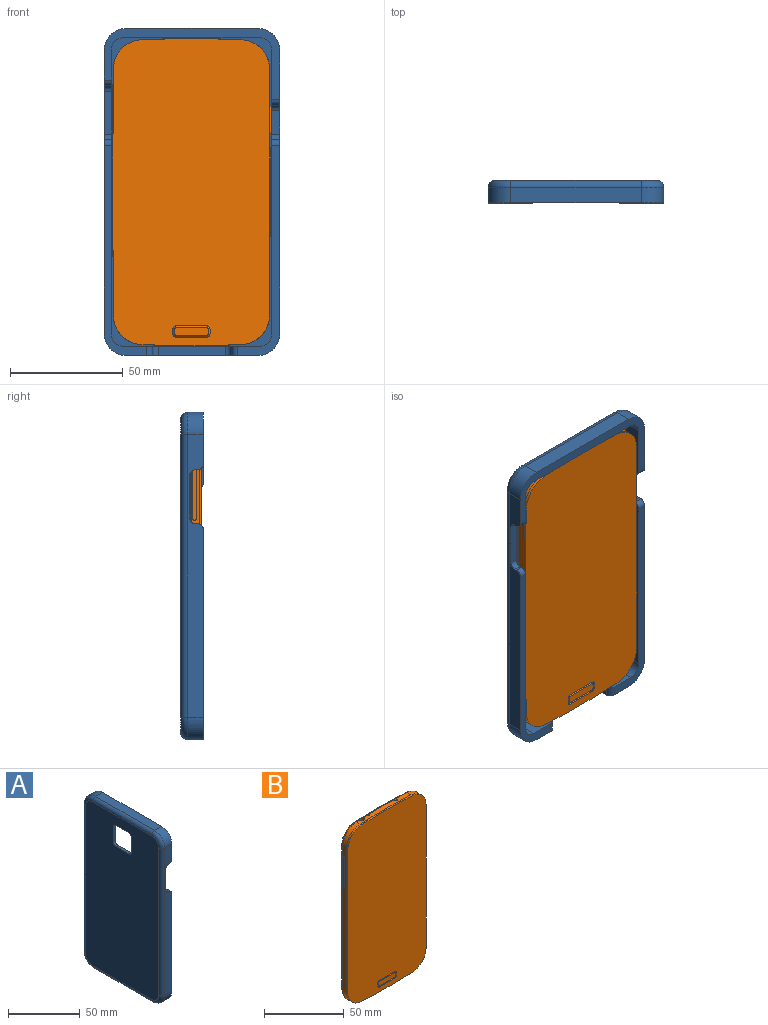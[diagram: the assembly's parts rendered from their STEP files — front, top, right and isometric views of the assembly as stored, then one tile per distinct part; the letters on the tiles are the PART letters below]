
ASSEMBLY  parts=2 mates=1
PART A: 59 faces, bbox 10x79.6x147.1 mm
  f0: plane 93.5x19mm, normal (1,0,0), area 354.7mm2, adj f1,f2,f5,f6,f16,f20,f47,f52
  f1: plane 12.5x7mm, normal (0,0,-1), area 79.8mm2, adj f0,f3,f20,f44,f47,f50
  f2: plane 61x8mm, normal (0,0,1), area 225.5mm2, adj f0,f7,f10,f16,f17,f44,f45,f46
  f3: cylinder r=3mm len=58mm, axis (0,1,0), area 257.2mm2, adj f1,f11,f13,f26,f29,f46,f49,f50
  f4: plane 78x31.7mm, normal (1,0,0), area 463.2mm2, adj f5,f6,f8,f9,f12,f14,f15,f18
  f5: plane 125.5x7mm, normal (0,-1,0), area 734.5mm2, adj f0,f4,f19,f20,f28,f41,f42,f43
  f6: plane 127x8mm, normal (0,1,0), area 872mm2, adj f0,f4,f10,f15,f16,f41,f42,f43
  f7: plane 93.5x19mm, normal (1,0,0), area 399.3mm2, adj f2,f8,f9,f13,f17,f21,f48,f55
  f8: plane 125.5x7mm, normal (0,1,0), area 786.7mm2, adj f4,f7,f21,f22,f24,f38,f39,f40
  f9: plane 127x8mm, normal (0,-1,0), area 924.2mm2, adj f4,f7,f10,f17,f18,f38,f39,f40
  f10: plane 137x71mm, normal (1,0,0), area 9389.3mm2, adj f2,f6,f9,f14,f15,f16,f17,f18
  f11: plane 139.5x72mm, normal (-1,0,0), area 9685.7mm2, adj f3,f23,f24,f25,f26,f27,f28,f29
  f12: plane 58x7mm, normal (0,0,1), area 406mm2, adj f4,f19,f22,f25
  f13: plane 12.5x7mm, normal (0,0,-1), area 79.8mm2, adj f3,f7,f21,f45,f48,f49
  f14: plane 61x8mm, normal (0,0,-1), area 488mm2, adj f4,f10,f15,f18
  f15: cylinder r=5mm len=8mm, axis (1,0,0), area 62.8mm2, adj f4,f6,f10,f14
  f16: cylinder r=5mm len=8mm, axis (-1,0,0), area 62.8mm2, adj f0,f2,f6,f10
  f17: cylinder r=5mm len=8mm, axis (1,0,0), area 62.8mm2, adj f2,f7,f9,f10
  f18: cylinder r=5mm len=8mm, axis (-1,0,0), area 62.8mm2, adj f4,f9,f10,f14
  f19: cylinder r=10mm len=10mm, axis (-1,0,0), area 110mm2, adj f4,f5,f12,f27
  f20: cylinder r=10mm len=10mm, axis (1,0,0), area 110mm2, adj f0,f1,f5,f29
  f21: cylinder r=10mm len=10mm, axis (1,0,0), area 110mm2, adj f7,f8,f13,f26
  f22: cylinder r=10mm len=10mm, axis (-1,0,0), area 110mm2, adj f4,f8,f12,f23
  f23: torus R=7mm, axis (1,0,0), area 66mm2, adj f11,f22,f24,f25
  f24: cylinder r=3mm len=125.5mm, axis (0,0,1), area 591.4mm2, adj f8,f11,f23,f26
  f25: cylinder r=3mm len=58mm, axis (0,-1,0), area 273.3mm2, adj f11,f12,f23,f27
  f26: torus R=7mm, axis (1,0,0), area 66mm2, adj f3,f11,f21,f24
  f27: torus R=7mm, axis (1,0,0), area 66mm2, adj f11,f19,f25,f28
  f28: cylinder r=3mm len=125.5mm, axis (0,0,-1), area 591.4mm2, adj f5,f11,f27,f29
  f29: torus R=7mm, axis (1,0,0), area 66mm2, adj f3,f11,f20,f28
  f30: plane 12x2mm, normal (0,0,-1), area 24mm2, adj f10,f11,f31,f37
  f31: cylinder r=3mm len=3mm, axis (1,0,0), area 9.4mm2, adj f10,f11,f30,f32
  f32: plane 12x2mm, normal (0,1,0), area 24mm2, adj f10,f11,f31,f33
  f33: cylinder r=3mm len=3mm, axis (1,0,0), area 9.4mm2, adj f10,f11,f32,f34
  f34: plane 12x2mm, normal (0,0,1), area 24mm2, adj f10,f11,f33,f35
  f35: cylinder r=3mm len=3mm, axis (1,0,0), area 9.4mm2, adj f10,f11,f34,f36
  f36: plane 12x2mm, normal (0,-1,0), area 24mm2, adj f10,f11,f35,f37
  f37: cylinder r=3mm len=3mm, axis (1,0,0), area 9.4mm2, adj f10,f11,f30,f36
  f38: plane 3.75x1mm, normal (0,0,1), area 3.7mm2, adj f8,f9,f55,f58
  f39: plane 3.75x1mm, normal (0,0,-1), area 3.8mm2, adj f8,f9,f56,f57
  f40: plane 10.3x3.75mm, normal (1,0,0), area 38.6mm2, adj f8,f9,f57,f58
  f41: plane 3.25x1mm, normal (0,0,-1), area 3.2mm2, adj f5,f6,f51,f53
  f42: plane 19x3.25mm, normal (1,0,0), area 61.8mm2, adj f5,f6,f53,f54
  f43: plane 3.25x1mm, normal (0,0,1), area 3.2mm2, adj f5,f6,f52,f54
  f44: plane 4.25x2.5mm, normal (0,1,0), area 10.6mm2, adj f1,f2,f47,f50
  f45: plane 4.25x2.5mm, normal (0,-1,0), area 10.6mm2, adj f2,f13,f48,f49
  f46: plane 30x4.21mm, normal (1,0,0), area 126.2mm2, adj f2,f3,f49,f50
  f47: cylinder r=2.5mm len=4.25mm, axis (0,0,1), area 16.7mm2, adj f0,f1,f2,f44
  f48: cylinder r=2.5mm len=4.25mm, axis (0,0,-1), area 16.7mm2, adj f2,f7,f13,f45
  f49: cylinder r=2.5mm len=4.25mm, axis (0,0,1), area 16.7mm2, adj f2,f3,f13,f45,f46
  f50: cylinder r=2.5mm len=4.25mm, axis (0,0,-1), area 16.7mm2, adj f1,f2,f3,f44,f46
  f51: cylinder r=2.5mm len=3.25mm, axis (0,1,0), area 12.8mm2, adj f4,f5,f6,f41
  f52: cylinder r=2.5mm len=3.25mm, axis (0,-1,0), area 12.8mm2, adj f0,f5,f6,f43
  f53: cylinder r=2.5mm len=3.25mm, axis (0,-1,0), area 12.8mm2, adj f5,f6,f41,f42
  f54: cylinder r=2.5mm len=3.25mm, axis (0,1,0), area 12.8mm2, adj f5,f6,f42,f43
  f55: cylinder r=2.5mm len=3.75mm, axis (0,-1,0), area 14.7mm2, adj f7,f8,f9,f38
  f56: cylinder r=2.5mm len=3.75mm, axis (0,1,0), area 14.7mm2, adj f4,f8,f9,f39
  f57: cylinder r=2.5mm len=3.75mm, axis (0,-1,0), area 14.7mm2, adj f8,f9,f39,f40
  f58: cylinder r=2.5mm len=3.75mm, axis (0,-1,0), area 14.7mm2, adj f8,f9,f38,f40
PART B: 126 faces, bbox 72.7x9.1x138.8 mm
  f0: cylinder r=0.94mm len=1.88mm, axis (0,0,1), area 1.6mm2, adj f73,f74,f75
  f1: cylinder r=0.99mm len=1.98mm, axis (0,0,1), area 1.7mm2, adj f5,f42,f73
  f2: cylinder r=0.38mm len=4.59mm, axis (0,0,-1), area 11mm2, adj f16,f72
  f3: cylinder r=0.38mm len=4.59mm, axis (0,0,1), area 11mm2, adj f5,f55
  f4: cylinder r=1.91mm len=4.42mm, axis (0,0,1), area 48.6mm2, adj f5,f9,f19,f42,f54
  f5: cone r=430.82mm half-angle=1deg, axis (0,-1,0), area 144.6mm2, adj f1,f3,f4,f6,f19,f33,f37,f42
  f6: cone r=430.8mm half-angle=1deg, axis (0,1,0), area 53mm2, adj f5,f10,f27,f32
  f7: cone r=430.8mm half-angle=1deg, axis (0,1,0), area 53mm2, adj f10,f16,f29,f30
  f8: torus R=425.67mm, axis (0,-1,0), area 264mm2, adj f13,f17,f18,f23,f24,f68,f69,f70
  f9: torus R=425.67mm, axis (0,-1,0), area 264.5mm2, adj f4,f13,f19,f21,f26,f42
  f10: plane 136.55x69.85mm, normal (0,-1,0), area 9235.6mm2, adj f6,f7,f27,f28,f29,f30,f31,f32
  f11: plane 1.65x0.76mm, normal (-1,0,0), area 0.9mm2, adj f13,f109,f110,f115,f117,f118,f119
  f12: plane 1.65x0.76mm, normal (1,0,0), area 0.9mm2, adj f13,f112,f113,f115,f117,f118,f119
  f13: plane 126.3x59.69mm, normal (0,1,0), area 7103.1mm2, adj f8,f9,f11,f12,f21,f22,f23,f24
  f14: plane 13.26x13.26mm, normal (0,1,0), area 167.1mm2, adj f101,f102,f103,f104,f105,f106,f107,f108
  f15: plane 16.51x5.08mm, normal (0,-1,0), area 3.1mm2, adj f76,f77,f78,f79,f80,f81,f82,f83
  f16: cone r=430.82mm half-angle=1deg, axis (0,-1,0), area 144.9mm2, adj f2,f7,f17,f18,f34,f35,f65,f66
  f17: torus R=429.74mm, axis (0,-1,0), area 9.3mm2, adj f8,f16,f38,f68
  f18: torus R=429.74mm, axis (0,-1,0), area 9.3mm2, adj f8,f16,f41,f70
  f19: torus R=429.74mm, axis (0,-1,0), area 1.1mm2, adj f4,f5,f9,f44
  f20: cone r=5935.77mm half-angle=1deg, axis (0,-1,0), area 359.9mm2, adj f28,f33,f34,f39,f45,f46,f47,f48
  f21: torus R=7.79mm, axis (0,-1,0), area 95.6mm2, adj f9,f13,f22,f44
  f22: torus R=5930.62mm, axis (0,-1,0), area 660.6mm2, adj f13,f21,f23,f43
  f23: torus R=7.79mm, axis (0,-1,0), area 95.6mm2, adj f8,f13,f22,f41
  f24: torus R=7.79mm, axis (0,-1,0), area 95.6mm2, adj f8,f13,f25,f38
  f25: torus R=5930.62mm, axis (0,-1,0), area 660.6mm2, adj f13,f24,f26,f39
  f26: torus R=7.79mm, axis (0,-1,0), area 95.6mm2, adj f9,f13,f25,f40
  f27: cone r=12.92mm half-angle=1deg, axis (0,1,0), area 23mm2, adj f6,f10,f28,f33
  f28: cone r=5935.75mm half-angle=1deg, axis (0,1,0), area 129.7mm2, adj f10,f20,f27,f29
  f29: cone r=12.92mm half-angle=1deg, axis (0,1,0), area 23mm2, adj f7,f10,f28,f34
  f30: cone r=12.92mm half-angle=1deg, axis (0,1,0), area 23mm2, adj f7,f10,f31,f35
  f31: cone r=5935.75mm half-angle=1deg, axis (0,1,0), area 129.7mm2, adj f10,f30,f32,f36
  f32: cone r=12.92mm half-angle=1deg, axis (0,1,0), area 23mm2, adj f6,f10,f31,f37
  f33: cone r=12.94mm half-angle=1deg, axis (0,-1,0), area 67mm2, adj f5,f20,f27,f40
  f34: cone r=12.94mm half-angle=1deg, axis (0,-1,0), area 67mm2, adj f16,f20,f29,f38
  f35: cone r=12.94mm half-angle=1deg, axis (0,-1,0), area 67mm2, adj f16,f30,f36,f41
  f36: cone r=5935.77mm half-angle=1deg, axis (0,-1,0), area 341.7mm2, adj f31,f35,f37,f43,f56,f57,f58,f59
  f37: cone r=12.94mm half-angle=1deg, axis (0,-1,0), area 67mm2, adj f5,f32,f36,f44
  f38: torus R=11.86mm, axis (0,-1,0), area 9.7mm2, adj f17,f24,f34,f39
  f39: torus R=5934.69mm, axis (0,-1,0), area 55.2mm2, adj f20,f25,f38,f40
  f40: torus R=11.86mm, axis (0,-1,0), area 9.7mm2, adj f26,f33,f39,f42
  f41: torus R=11.86mm, axis (0,-1,0), area 9.7mm2, adj f18,f23,f35,f43
  f42: torus R=429.74mm, axis (0,1,0), area 19.5mm2, adj f1,f4,f5,f9,f40
  f43: torus R=5934.69mm, axis (0,-1,0), area 55.2mm2, adj f22,f36,f41,f44
  f44: torus R=11.86mm, axis (0,-1,0), area 9.7mm2, adj f19,f21,f37,f43
  f45: bspline ~0.82x0.81mm, area 0.7mm2, adj f20,f46,f52,f53
  f46: plane 10.23x0.62mm, normal (0,-1,0), area 5.7mm2, adj f20,f45,f47,f53
  f47: bspline ~0.82x0.81mm, area 0.7mm2, adj f20,f46,f51,f53
  f48: bspline ~0.81x0.81mm, area 0.7mm2, adj f20,f49,f51,f53
  f49: plane 10.23x0.62mm, normal (0,1,0), area 5.7mm2, adj f20,f48,f50,f53
  f50: bspline ~0.81x0.81mm, area 0.7mm2, adj f20,f49,f52,f53
  f51: plane 0.56x0.01mm, normal (0,0,1), area 0mm2, adj f47,f48
  f52: plane 0.56x0.01mm, normal (0,0,-1), area 0mm2, adj f45,f50
  f53: bspline ~12.09x1.66mm, area 17.9mm2, adj f45,f46,f47,f48,f49,f50
  f54: plane 3.81x3.81mm, normal (0,0,1), area 11.4mm2, adj f4
  f55: plane 0.76x0.76mm, normal (0,0,1), area 0.5mm2, adj f3
  f56: bspline ~0.81x0.81mm, area 0.5mm2, adj f36,f57,f63,f64
  f57: plane 21.42x0.51mm, normal (0,1,0), area 8.2mm2, adj f36,f56,f58,f64
  f58: bspline ~0.81x0.81mm, area 0.5mm2, adj f36,f57,f62,f64
  f59: bspline ~0.81x0.81mm, area 0.5mm2, adj f36,f60,f62,f64
  f60: plane 21.42x0.51mm, normal (0,-1,0), area 8.2mm2, adj f36,f59,f61,f64
  f61: bspline ~0.82x0.81mm, area 0.5mm2, adj f36,f60,f63,f64
  f62: plane 0.38x0.01mm, normal (0,0,-1), area 0mm2, adj f58,f59
  f63: plane 0.39x0.01mm, normal (0,0,1), area 0mm2, adj f56,f61
  f64: bspline ~23.5x1.66mm, area 36.1mm2, adj f56,f57,f58,f59,f60,f61
  f65: plane 4.75x0.92mm, normal (0.69,0.72,0), area 6.1mm2, adj f16,f66,f70,f71
  f66: plane 6.1x4.75mm, normal (0,1,0), area 24.7mm2, adj f16,f65,f67,f71,f120,f122,f123
  f67: plane 4.75x0.92mm, normal (-0.69,0.72,0), area 6.1mm2, adj f16,f66,f68,f71
  f68: plane 4.72x1.27mm, normal (-1,0,0), area 5.8mm2, adj f8,f16,f17,f67,f69,f71
  f69: plane 7.94x4.3mm, normal (0,-1,0), area 34.1mm2, adj f8,f68,f70,f71
  f70: plane 4.72x1.27mm, normal (1,0,0), area 5.8mm2, adj f8,f16,f18,f65,f69,f71
  f71: plane 7.94x2.16mm, normal (0,0,-1), area 16.3mm2, adj f65,f66,f67,f68,f69,f70
  f72: plane 0.76x0.76mm, normal (0,0,-1), area 0.5mm2, adj f2
  f73: plane 1.98x1.98mm, normal (0,0,1), area 0.3mm2, adj f0,f1
  f74: torus R=429.74mm, axis (0,1,0), area 0.1mm2, adj f0,f75
  f75: cone r=430.82mm half-angle=1deg, axis (0,-1,0), area 2.5mm2, adj f0,f74
  f76: cylinder r=1.52mm len=1.52mm, axis (0,-1,0), area 3mm2, adj f10,f15,f77,f83
  f77: plane 13.46x1.27mm, normal (0,0,1), area 17.1mm2, adj f10,f15,f76,f78
  f78: cylinder r=1.52mm len=1.52mm, axis (0,-1,0), area 3mm2, adj f10,f15,f77,f79
  f79: plane 2.03x1.27mm, normal (1,0,0), area 2.6mm2, adj f10,f15,f78,f80
  f80: cylinder r=1.52mm len=1.52mm, axis (0,-1,0), area 3mm2, adj f10,f15,f79,f81
  f81: plane 13.46x1.27mm, normal (0,0,-1), area 17.1mm2, adj f10,f15,f80,f82
  f82: cylinder r=1.52mm len=1.52mm, axis (0,-1,0), area 3mm2, adj f10,f15,f81,f83
  f83: plane 2.03x1.27mm, normal (-1,0,0), area 2.6mm2, adj f10,f15,f76,f82
  f84: cylinder r=1.45mm len=1.45mm, axis (0,1,0), area 1.2mm2, adj f15,f85,f91,f96
  f85: plane 2.03x0.51mm, normal (1,0,0), area 1mm2, adj f15,f84,f86,f98
  f86: cylinder r=1.45mm len=1.45mm, axis (0,1,0), area 1.2mm2, adj f15,f85,f87,f100
  f87: plane 13.46x0.51mm, normal (0,0,1), area 6.8mm2, adj f15,f86,f88,f99
  f88: cylinder r=1.45mm len=1.45mm, axis (0,1,0), area 1.2mm2, adj f15,f87,f89,f97
  f89: plane 2.03x0.51mm, normal (-1,0,0), area 1mm2, adj f15,f88,f90,f95
  f90: cylinder r=1.45mm len=1.45mm, axis (0,1,0), area 1.2mm2, adj f15,f89,f91,f93
  f91: plane 13.46x0.51mm, normal (0,0,-1), area 6.8mm2, adj f15,f84,f90,f94
  f92: plane 14.83x3.4mm, normal (0,-1,0), area 50.1mm2, adj f93,f94,f95,f96,f97,f98,f99,f100
  f93: cone r=0.69mm half-angle=45deg, axis (0,1,0), area 1.8mm2, adj f90,f92,f94,f95
  f94: plane 13.46x0.76mm, normal (0,-0.71,-0.71), area 14.5mm2, adj f91,f92,f93,f96
  f95: plane 2.03x0.76mm, normal (-0.71,-0.71,0), area 2.2mm2, adj f89,f92,f93,f97
  f96: cone r=0.69mm half-angle=45deg, axis (0,1,0), area 1.8mm2, adj f84,f92,f94,f98
  f97: cone r=0.69mm half-angle=45deg, axis (0,1,0), area 1.8mm2, adj f88,f92,f95,f99
  f98: plane 2.03x0.76mm, normal (0.71,-0.71,0), area 2.2mm2, adj f85,f92,f96,f100
  f99: plane 13.46x0.76mm, normal (0,-0.71,0.71), area 14.5mm2, adj f87,f92,f97,f100
  f100: cone r=0.69mm half-angle=45deg, axis (0,1,0), area 1.8mm2, adj f86,f92,f98,f99
  f101: torus R=5.46mm, axis (0,-1,0), area 16.5mm2, adj f13,f14,f102,f108
  f102: cylinder r=3.81mm len=6.91mm, axis (0,0,-1), area 16.9mm2, adj f13,f14,f101,f103
  f103: torus R=5.46mm, axis (0,-1,0), area 16.5mm2, adj f13,f14,f102,f104
  f104: cylinder r=3.81mm len=6.91mm, axis (-1,0,0), area 16.9mm2, adj f13,f14,f103,f105
  f105: torus R=5.46mm, axis (0,-1,0), area 16.5mm2, adj f13,f14,f104,f106
  f106: cylinder r=3.81mm len=6.91mm, axis (0,0,1), area 16.9mm2, adj f13,f14,f105,f107
  f107: torus R=5.46mm, axis (0,-1,0), area 16.5mm2, adj f13,f14,f106,f108
  f108: cylinder r=3.81mm len=6.91mm, axis (-1,0,0), area 16.9mm2, adj f13,f14,f101,f107
  f109: cylinder r=0.76mm len=0.76mm, axis (0,1,0), area 0.9mm2, adj f11,f13,f114,f115
  f110: cylinder r=0.76mm len=0.76mm, axis (0,1,0), area 0.9mm2, adj f11,f13,f111,f115
  f111: plane 4.83x0.76mm, normal (0,0,-1), area 3.7mm2, adj f13,f110,f112,f115
  f112: cylinder r=0.76mm len=0.76mm, axis (0,1,0), area 0.9mm2, adj f12,f13,f111,f115
  f113: cylinder r=0.76mm len=0.76mm, axis (0,1,0), area 0.9mm2, adj f12,f13,f114,f115
  f114: plane 4.83x0.76mm, normal (0,0,1), area 3.7mm2, adj f13,f109,f113,f115
  f115: plane 6.35x3.18mm, normal (0,1,0), area 19.7mm2, adj f11,f12,f109,f110,f111,f112,f113,f114
  f116: cylinder r=8.56mm len=6.35mm, axis (0,0,-1), area 7.6mm2, adj f13,f118,f119
  f117: cylinder r=8.31mm len=6.35mm, axis (0,0,-1), area 7.6mm2, adj f11,f12,f118,f119
  f118: plane 6.35x0.88mm, normal (0,0,1), area 1.7mm2, adj f11,f12,f116,f117
  f119: plane 6.35x0.88mm, normal (0,0,-1), area 1.7mm2, adj f11,f12,f116,f117
  f120: plane 1.7x0.25mm, normal (1,0,0), area 0.2mm2, adj f16,f66,f121,f123,f124,f125
  f121: plane 2.79x0.25mm, normal (0,0,-1), area 0.7mm2, adj f120,f122,f124,f125
  f122: plane 1.7x0.25mm, normal (-1,0,0), area 0.2mm2, adj f16,f66,f121,f123,f124,f125
  f123: plane 2.79x0.13mm, normal (0,0,1), area 0.4mm2, adj f66,f120,f122,f124
  f124: plane 2.79x1.7mm, normal (0,1,0), area 4.7mm2, adj f120,f121,f122,f123
  f125: plane 2.79x0.17mm, normal (0,-1,0), area 0.5mm2, adj f16,f120,f121,f122
PLACE A rot(axis=(0,0,-1),90deg) t=(59.75,60.36,38.95)mm
PLACE B t=(59.5,55.94,38.87)mm fixed
MATE fastened A.f2 <-> B.f121  axis (0,0,1) through (59.5,59.36,-29.55)mm
